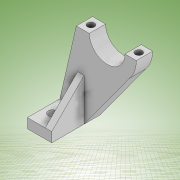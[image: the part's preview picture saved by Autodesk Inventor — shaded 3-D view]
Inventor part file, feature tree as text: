
AUTODESK INVENTOR PART (.ipt)
format: ipt  version: 2022 (Build 260153000, 153)  size: 172,544 bytes
history: native  units: mm
features: sketch x6, extrude x5, other x2
ambient origin geometry x8: Origin, YZ Plane, XZ Plane, XY Plane, X Axis, Y Axis, Z Axis, Center Point
bodies: Body1 (feature_tree)
feature tree (13):
  other  "Sólido1"
  extrude  "Extrusión1"  Depth=50.0mm
  extrude  "Extrusión2"  Depth=6.0mm
  other  "Nervio1"
  extrude  "Extrusión3"  Depth=37.0mm
  extrude  "Extrusión4"  Depth=15.0mm
  extrude  "Extrusión5"  Depth=20.0mm TaperAngle=0.0deg
  sketch  "Boceto1"  dims[d3=50.0mm d4=22.0mm]
  sketch  "Boceto2"  dims[d5=6.0mm d6=21.991149mm]
  sketch  "Boceto3"  dims[d10=13.439035mm d12=37.0mm]
  sketch  "Boceto4"  dims[d13=8.0mm d15=15.0mm]
  sketch  "Boceto5"  dims[d16=10.0mm d17=0.0mm d18=20.0mm d19=0.0mm]
  sketch  "Boceto6"  dims[d20=45.0deg d21=1.0mm d22=4.0mm d23=0.0mm d24=0.0mm d25=1.0mm d26=1.0mm d27=5.3mm d28=10.0mm d29=5.5mm d30=0.0mm d31=0.0mm d32=4.3mm d33=4.0mm d34=0.0mm d35=4.3mm d36=4.0mm d37=0.0mm]
